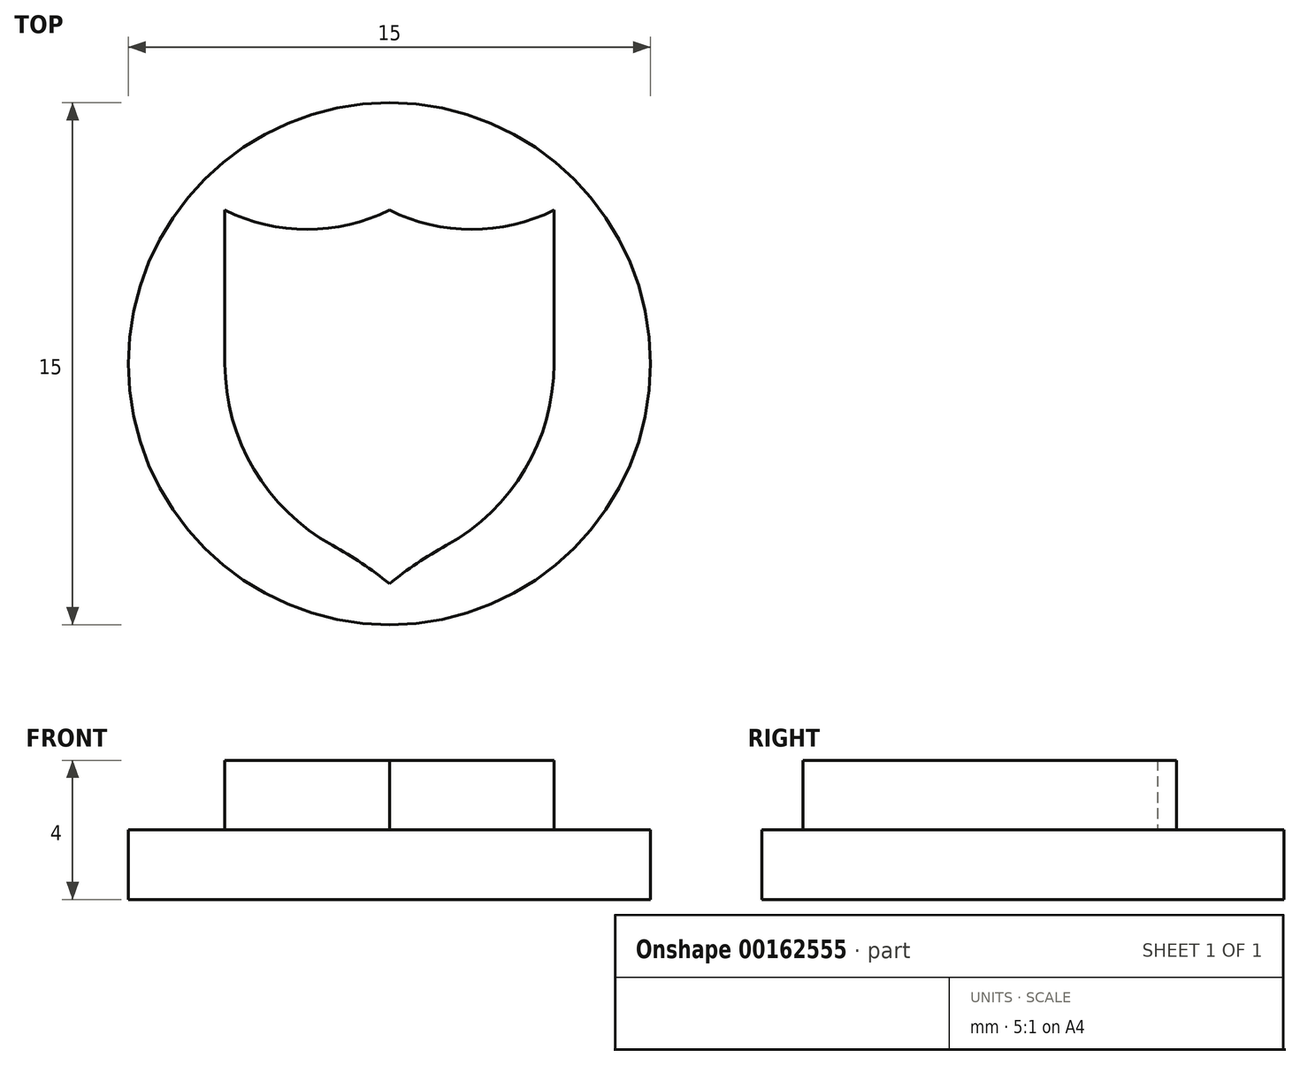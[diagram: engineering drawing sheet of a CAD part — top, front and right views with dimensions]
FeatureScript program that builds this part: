
annotation { "Feature Type Name" : "Feature", "Feature Type Description" : "" }
export const myFeature = defineFeature(function(context is Context, id is Id, definition is map)
    precondition{}
    {
        {
            var Q0;
            Q0=qCreatedBy(makeId("Top.planeOp"),FACE);
            var sketch = newSketch(context, id + "F0", { "sketchPlane" : qUnion([Q0])});
            skCircle(sketch, "E0", {"center": v(0, 0) * mm, "radius": 7.5 * mm});
            skSolve(sketch);
        }
        {
            var Q0;
            Q0 = qSketchRegion(id + "F0", true);
            extrude(context, id + "F1", {"entities" : qUnion([Q0]), "depth" : 2 * mm});
        }
        {
            var Q0;
            Q0=makeQuery(id+"F1.opExtrude","CAP_FACE",FACE,{"disambiguationData":[OSD([sQuery(id+"F0.wireOp",EDGE,"E0")])],"isStart":false});
            var sketch = newSketch(context, id + "F2", { "sketchPlane" : qUnion([Q0])});
            skLineSegment(sketch, "E1", {"start": v(0, 9.65) * mm, "end": v(0, -10.58) * mm, "construction": true});
            skArc(sketch, "E2", {"start": v(0, -6.32) * mm, "mid": v(-0.8, -5.74) * mm, "end": v(-1.63, -5.22) * mm});
            skArc(sketch, "E3", {"start": v(-4.73, 0) * mm, "mid": v(-3.9, -3.03) * mm, "end": v(-1.63, -5.22) * mm});
            skLineSegment(sketch, "E4", {"start": v(-4.73, 0) * mm, "end": v(-4.73, 4.42) * mm});
            skArc(sketch, "E5", {"start": v(-4.73, 4.42) * mm, "mid": v(-2.36, 3.86) * mm, "end": v(0, 4.42) * mm});
            skArc(sketch, "E6.MirrorCS", {"start": v(4.73, 4.42) * mm, "mid": v(2.36, 3.86) * mm, "end": v(0, 4.42) * mm});
            skLineSegment(sketch, "E7.MirrorCS", {"start": v(4.73, 0) * mm, "end": v(4.73, 4.42) * mm});
            skArc(sketch, "E8.MirrorCS", {"start": v(4.73, 0) * mm, "mid": v(3.9, -3.03) * mm, "end": v(1.63, -5.22) * mm});
            skArc(sketch, "E9.MirrorCS", {"start": v(0, -6.32) * mm, "mid": v(0.8, -5.74) * mm, "end": v(1.63, -5.22) * mm});
            skSolve(sketch);
        }
        {
            var Q0;
            Q0 = qSketchRegion(id + "F2", true);
            extrude(context, id + "F3", {"entities" : qUnion([Q0]), "operationType" : NewBodyOperationType.ADD, "depth" : 2 * mm});
        }
    });
